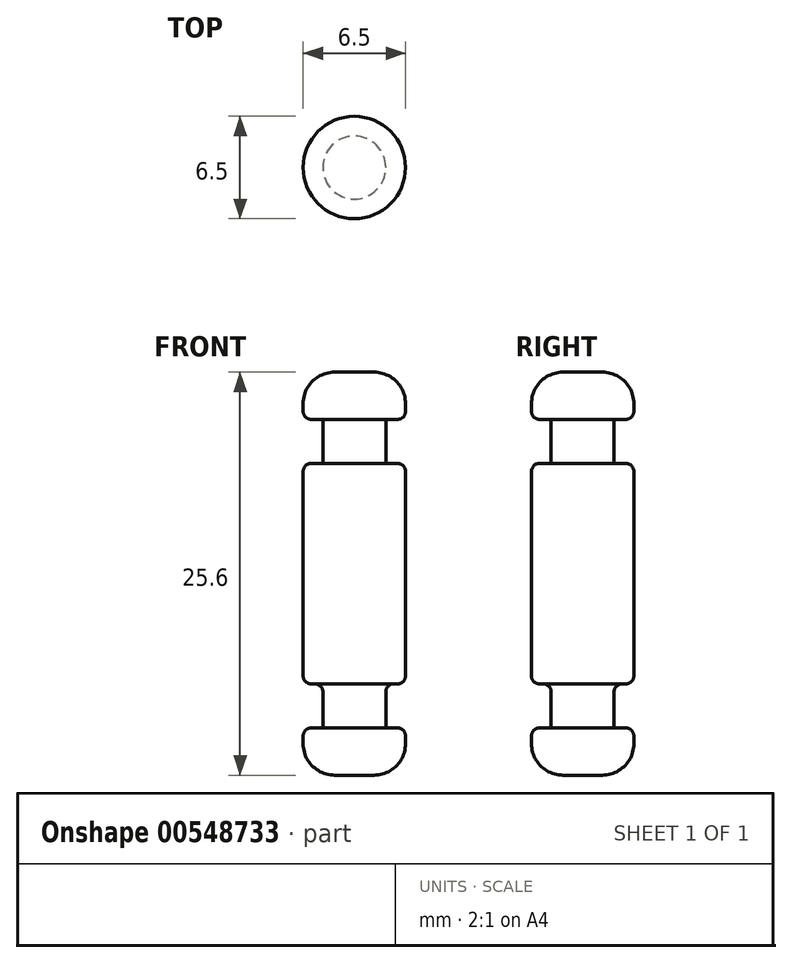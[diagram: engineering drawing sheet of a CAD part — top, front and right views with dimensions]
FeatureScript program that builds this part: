
annotation { "Feature Type Name" : "Feature", "Feature Type Description" : "" }
export const myFeature = defineFeature(function(context is Context, id is Id, definition is map)
    precondition{}
    {
        {
            var Q0;
            Q0=qCreatedBy(makeId("Top.planeOp"),FACE);
            var sketch = newSketch(context, id + "F0", { "sketchPlane" : qUnion([Q0])});
            skCircle(sketch, "E0", {"center": v(0, 0) * mm, "radius": 3.25 * mm});
            skCircle(sketch, "E1", {"center": v(0, 0) * mm, "radius": 2 * mm});
            skSolve(sketch);
        }
        {
            var Q0;
            Q0=makeQuery(id+"F0.imprint","IMPRINT",FACE,{"disambiguationData":[TD([[makeQuery(id+"F0.imprint","IMPRINT",EDGE,{"derivedFrom":sQuery(id+"F0.wireOp",EDGE,"E1")}),1.0]])]});
            extrude(context, id + "F1", {"entities" : qUnion([Q0]), "depth" : 9.8 * mm, "hasSecondDirection" : true, "secondDirectionOppositeDirection" : true, "secondDirectionDepth" : 9.8 * mm});
        }
        {
            var Q0;
            Q0=qSketchRegion(id+"F0",true);
            extrude(context, id + "F2", {"entities" : qUnion([Q0]), "operationType" : NewBodyOperationType.ADD, "depth" : 7 * mm, "hasSecondDirection" : true, "secondDirectionOppositeDirection" : true, "secondDirectionDepth" : 7 * mm});
        }
        {
            var Q0;
            Q0=makeQuery(id+"F1.opExtrude","CAP_FACE",FACE,{"disambiguationData":[OSD([sQuery(id+"F0.wireOp",EDGE,"E1")])],"isStart":true});
            var sketch = newSketch(context, id + "F3", { "sketchPlane" : qUnion([Q0])});
            skCircle(sketch, "E2", {"center": v(0, 0) * mm, "radius": 3.25 * mm});
            skSolve(sketch);
        }
        {
            var Q0;
            Q0=makeQuery(id+"F1.opExtrude","CAP_FACE",FACE,{"disambiguationData":[OSD([sQuery(id+"F0.wireOp",EDGE,"E1")])],"isStart":false});
            var sketch = newSketch(context, id + "F4", { "sketchPlane" : qUnion([Q0])});
            skCircle(sketch, "E3", {"center": v(0, 0) * mm, "radius": 3.25 * mm});
            skSolve(sketch);
        }
        {
            var Q0;
            Q0=qSketchRegion(id+"F4",true);
            extrude(context, id + "F5", {"entities" : qUnion([Q0]), "operationType" : NewBodyOperationType.ADD, "depth" : 3 * mm});
        }
        {
            var Q0;
            Q0=qSketchRegion(id+"F3",true);
            extrude(context, id + "F6", {"entities" : qUnion([Q0]), "operationType" : NewBodyOperationType.ADD, "depth" : 3 * mm});
        }
        {
            var Q0;
            Q0=makeQuery(id+"F5.opExtrude","CAP_EDGE",EDGE,{"disambiguationData":[OSD([sQuery(id+"F4.wireOp",EDGE,"E3")])],"isStart":false});
            var Q1;
            Q1=makeQuery(id+"F6.opExtrude","CAP_EDGE",EDGE,{"disambiguationData":[OSD([sQuery(id+"F3.wireOp",EDGE,"E2")])],"isStart":false});
            fillet(context, id + "F7", {"entities" : qUnion([Q0, Q1]), "radius" : 2 * mm, "tangentPropagation" : true, "allowEdgeOverflow" : false});
        }
        {
            var Q0;
            {var subQ0=sQuery(id+"F4.wireOp",EDGE,"E3");Q0=makeQuery(id+"F7.opFillet","BLEND_EDGE",EDGE,{"blendedFrom":[makeQuery(id+"F5.opExtrude","CAP_EDGE",EDGE,{"disambiguationData":[OSD([subQ0])],"isStart":false}),makeQuery(id+"F5.opExtrude","CAP_FACE",FACE,{"disambiguationData":[OSD([subQ0])],"isStart":true})],"blendedInto":[makeQuery(id+"F5.opExtrude","CAP_FACE",FACE,{"disambiguationData":[OSD([subQ0])],"isStart":true})]});}
            var Q1;
            Q1=makeQuery(id+"F2.opExtrude","CAP_EDGE",EDGE,{"disambiguationData":[OSD([sQuery(id+"F0.wireOp",EDGE,"E0")])],"isStart":false});
            var Q2;
            Q2=makeQuery(id+"F2.opExtrude","CAP_EDGE",EDGE,{"disambiguationData":[OSD([sQuery(id+"F0.wireOp",EDGE,"E0")])],"isStart":true});
            var Q3;
            {var subQ0=sQuery(id+"F3.wireOp",EDGE,"E2");Q3=makeQuery(id+"F7.opFillet","BLEND_EDGE",EDGE,{"blendedFrom":[makeQuery(id+"F6.opExtrude","CAP_EDGE",EDGE,{"disambiguationData":[OSD([subQ0])],"isStart":false}),makeQuery(id+"F6.opExtrude","CAP_FACE",FACE,{"disambiguationData":[OSD([subQ0])],"isStart":true})],"blendedInto":[makeQuery(id+"F6.opExtrude","CAP_FACE",FACE,{"disambiguationData":[OSD([subQ0])],"isStart":true})]});}
            var Q4;
            Q4=makeQuery(id+"F1.opExtrude","CAP_EDGE",EDGE,{"disambiguationData":[OSD([sQuery(id+"F0.wireOp",EDGE,"E1")])],"isStart":true});
            var Q5;
            Q5=makeQuery(id+"F2.opExtrude","CAP_EDGE",EDGE,{"disambiguationData":[OSD([sQuery(id+"F0.wireOp",EDGE,"E1")])],"isStart":true});
            var Q6;
            Q6=makeQuery(id+"F1.opExtrude","CAP_EDGE",EDGE,{"disambiguationData":[OSD([sQuery(id+"F0.wireOp",EDGE,"E1")])],"isStart":false});
            var Q7;
            Q7=makeQuery(id+"F2.opExtrude","CAP_EDGE",EDGE,{"disambiguationData":[OSD([sQuery(id+"F0.wireOp",EDGE,"E1")])],"isStart":false});
            var Q8;
            Q8=makeQuery(id+"F5.opExtrude","CAP_EDGE",EDGE,{"disambiguationData":[OSD([sQuery(id+"F4.wireOp",EDGE,"E3")])],"isStart":true});
            var Q9;
            Q9=makeQuery(id+"F6.opExtrude","CAP_EDGE",EDGE,{"disambiguationData":[OSD([sQuery(id+"F3.wireOp",EDGE,"E2")])],"isStart":true});
            fillet(context, id + "F8", {"entities" : qUnion([Q0, Q1, Q2, Q3, Q4, Q5, Q6, Q7, Q8, Q9]), "radius" : .5 * mm, "tangentPropagation" : true, "allowEdgeOverflow" : false});
        }
    });
